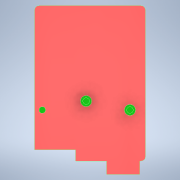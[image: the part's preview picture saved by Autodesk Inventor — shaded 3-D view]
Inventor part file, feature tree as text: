
AUTODESK INVENTOR PART (.ipt)
format: ipt  version: 2022 (Build 260153000, 153)  size: 167,936 bytes
history: native  units: mm
features: extrude x6, sketch x4, fillet x1
ambient origin geometry x8: Origin, YZ Plane, XZ Plane, XY Plane, X Axis, Y Axis, Z Axis, Center Point
bodies: Body1 (feature_tree)
feature tree (11):
  extrude  "Extrusion3"  Depth=70.0mm
  fillet  "Fillet1"  Radius=6.0mm
  sketch  "Sketch4"  dims[d14=2.0mm d16=18.5mm]
  extrude  "Extrusion5"  Depth=18.5mm
  extrude  "Extrusion6"  Depth=5.0mm
  extrude  "Extrusion7"  Depth=40.0mm TaperAngle=0.0deg
  extrude  "Extrusion8"  Depth=5.0mm
  extrude  "Extrusion9"  Depth=6.0mm
  sketch  "Sketch2"  dims[d0=50.0mm d1=70.0mm d12=6.0mm d13=0.0mm]
  sketch  "Sketch5"  dims[d17=5.0mm d31=5.0mm]
  sketch  "Sketch6"  dims[d34=3.0mm d37=40.0mm d38=0.0mm d41=5.0mm d44=19.75mm d45=19.75mm d46=7.0mm d48=5.6mm d49=0.0mm d50=3.0mm d51=34.4mm d52=0.0mm d53=10.64mm d54=0.0mm d55=3.0mm d56=29.36mm d57=0.0mm d58=2.5mm d59=15.0mm d60=6.0mm d61=23.0mm d62=27.0mm d63=23.0mm d4=0.0mm d5=0.0mm d6=0.0mm d7=0.0mm]
